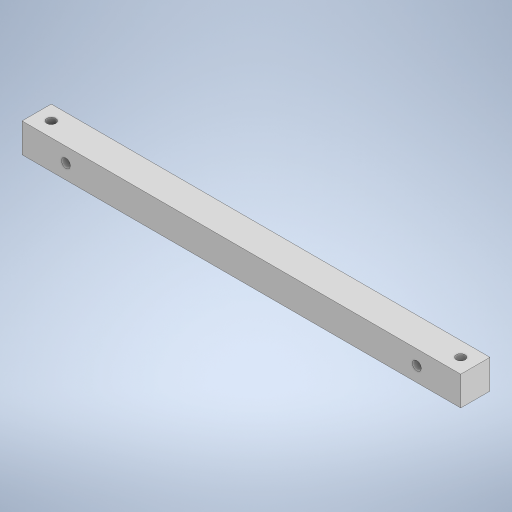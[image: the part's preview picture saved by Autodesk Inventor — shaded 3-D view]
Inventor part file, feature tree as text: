
AUTODESK INVENTOR PART (.ipt)
format: ipt  version: 2023 (Build 270158000, 158)  size: 242,688 bytes
history: native  units: mm
features: sketch x3, hole x2, other x1, extrude x1
ambient origin geometry x8: Origin, YZ Plane, XZ Plane, XY Plane, X Axis, Y Axis, Z Axis, Center Point
bodies: Body1 (feature_tree)
feature tree (7):
  other  "ソリッド1"
  extrude  "押し出し1"  Depth=150.0mm
  hole  "穴1"  [1 undecoded]
  hole  "穴2"  [1 undecoded]
  sketch  "スケッチ1"
  sketch  "スケッチ2"
  sketch  "スケッチ3"
note: 2 required parameter values undecoded (feature->parameter linkage not recoverable at this tier; creation-order binding heuristic only, values carry confidence <= 0.55)
